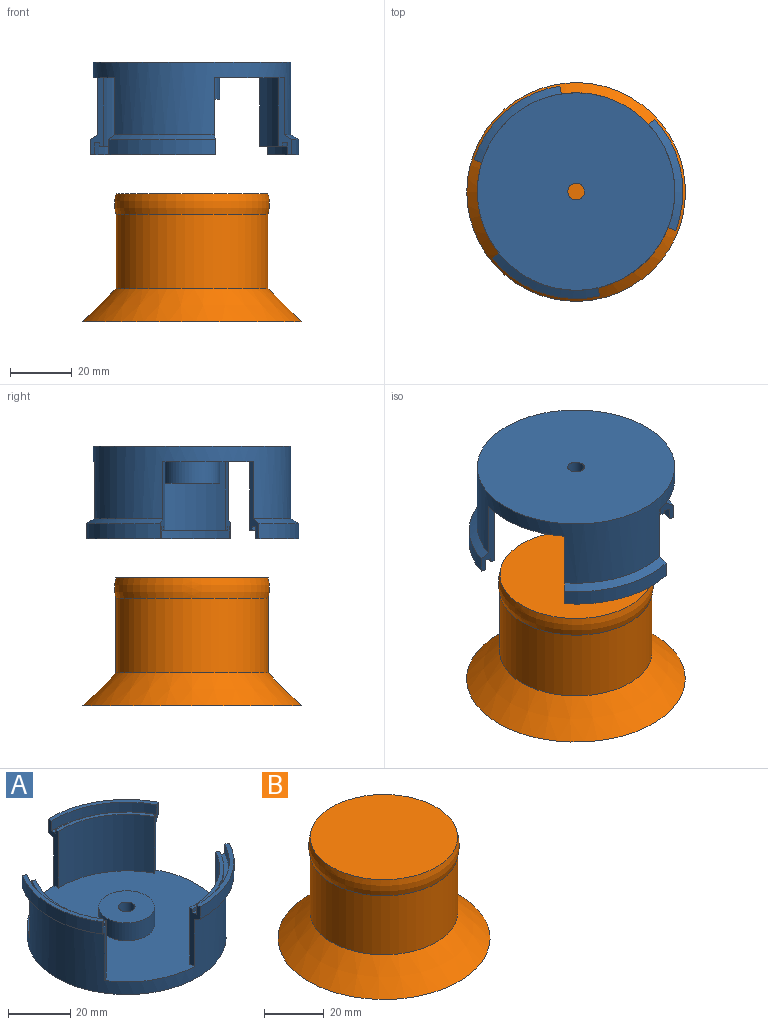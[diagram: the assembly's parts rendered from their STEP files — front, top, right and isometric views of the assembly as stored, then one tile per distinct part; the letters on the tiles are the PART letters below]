
ASSEMBLY  parts=2 mates=1
PART A: 36 faces, bbox 66.6x69.2x29.9 mm
  f0: cone r=34.61mm half-angle=59deg, axis (0,0,1), area 113.5mm2, adj f2,f17,f30,f35
  f1: cone r=34.61mm half-angle=59deg, axis (0,0,1), area 113.5mm2, adj f3,f17,f33,f34
  f2: cylinder r=34.61mm len=31.73mm, axis (0,0,-1), area 187.9mm2, adj f0,f4,f30,f35
  f3: cylinder r=34.61mm len=31.73mm, axis (0,0,-1), area 187.9mm2, adj f1,f5,f33,f34
  f4: plane 31.73x19.11mm, normal (0,0,1), area 58.4mm2, adj f2,f6,f30,f35
  f5: plane 31.73x19.11mm, normal (0,0,1), area 58.4mm2, adj f3,f7,f33,f34
  f6: cylinder r=33.07mm len=30.39mm, axis (0,0,-1), area 143mm2, adj f4,f8,f30,f35
  f7: cylinder r=33.07mm len=30.39mm, axis (0,0,-1), area 143mm2, adj f5,f9,f33,f34
  f8: plane 30.39x18.43mm, normal (0,0,1), area 62.4mm2, adj f6,f10,f30,f35
  f9: plane 30.39x18.43mm, normal (0,0,1), area 62.4mm2, adj f7,f11,f33,f34
  f10: cylinder r=31.34mm len=28.89mm, axis (0,0,-1), area 43.6mm2, adj f8,f12,f30,f35
  f11: cylinder r=31.34mm len=28.89mm, axis (0,0,-1), area 43.6mm2, adj f9,f13,f33,f34
  f12: plane 28.89x17.37mm, normal (0,0,1), area 46.1mm2, adj f10,f14,f30,f35
  f13: plane 28.89x17.37mm, normal (0,0,1), area 46.1mm2, adj f11,f15,f33,f34
  f14: cylinder r=30mm len=27.73mm, axis (0,0,-1), area 753.4mm2, adj f12,f26,f30,f35
  f15: cylinder r=30mm len=27.73mm, axis (0,0,-1), area 753.4mm2, adj f13,f26,f33,f34
  f16: plane 64x64mm, normal (0,0,-1), area 3194.1mm2, adj f17,f29
  f17: cylinder r=32mm len=64mm, axis (0,0,-1), area 2995.5mm2, adj f0,f1,f16,f18,f26,f30,f31,f32
  f18: cone r=34.61mm half-angle=59deg, axis (0,0,1), area 113.5mm2, adj f17,f19,f31,f32
  f19: cylinder r=34.61mm len=36.64mm, axis (0,0,-1), area 187.9mm2, adj f18,f20,f31,f32
  f20: plane 36.64x6.58mm, normal (0,0,1), area 58.4mm2, adj f19,f21,f31,f32
  f21: cylinder r=33.07mm len=35.09mm, axis (0,0,-1), area 143mm2, adj f20,f22,f31,f32
  f22: plane 35.09x6.54mm, normal (0,0,1), area 62.4mm2, adj f21,f23,f31,f32
  f23: cylinder r=31.34mm len=33.36mm, axis (0,0,-1), area 43.6mm2, adj f22,f24,f31,f32
  f24: plane 33.36x5.97mm, normal (0,0,1), area 46.1mm2, adj f23,f25,f31,f32
  f25: cylinder r=30mm len=32.02mm, axis (0,0,-1), area 753.4mm2, adj f24,f26,f31,f32
  f26: plane 63.96x62mm, normal (0,0,1), area 2753.6mm2, adj f14,f15,f17,f25,f27,f30,f31,f32
  f27: cylinder r=9mm len=18mm, axis (0,0,-1), area 395.8mm2, adj f26,f28
  f28: plane 18x18mm, normal (0,0,1), area 231.6mm2, adj f27,f29
  f29: cylinder r=2.7mm len=12mm, axis (0,0,-1), area 203.6mm2, adj f16,f28
  f30: plane 24.94x4.62mm, normal (-1,0,0), area 54.5mm2, adj f0,f2,f4,f6,f8,f10,f12,f14
  f31: plane 24.94x4mm, normal (0.5,-0.87,0), area 54.5mm2, adj f17,f18,f19,f20,f21,f22,f23,f24
  f32: plane 24.94x4mm, normal (0.5,0.87,0), area 54.5mm2, adj f17,f18,f19,f20,f21,f22,f23,f24
  f33: plane 24.94x4.62mm, normal (-1,0,0), area 54.5mm2, adj f1,f3,f5,f7,f9,f11,f13,f15
  f34: plane 24.94x4mm, normal (0.5,-0.87,0), area 54.5mm2, adj f1,f3,f5,f7,f9,f11,f13,f15
  f35: plane 24.94x4mm, normal (0.5,0.87,0), area 54.5mm2, adj f0,f2,f4,f6,f8,f10,f12,f14
PART B: 5 faces, bbox 70.9x70.9x41.4 mm
  f0: plane 70.87x70.87mm, normal (0,0,-1), area 3944.3mm2, adj f1
  f1: cone r=35.43mm half-angle=45.3deg, axis (0,0,-1), area 2864.2mm2, adj f0,f2
  f2: cylinder r=24.64mm len=49.28mm, axis (0,0,-1), area 3735.4mm2, adj f1,f3
  f3: torus R=14.16mm, axis (0,0,-1), area 1052.6mm2, adj f2,f4
  f4: plane 49.28x49.28mm, normal (0,0,1), area 1907mm2, adj f3
PLACE A rot(axis=(0.91,-0.42,0),180deg) t=(-31.52,-2.59,86.81)mm
PLACE B t=(-31.52,-2.59,2.71)mm fixed
MATE cylindrical A.f0 <-> B.f1  axis (0,0,-1) through (-31.52,-2.59,74.81)mm
